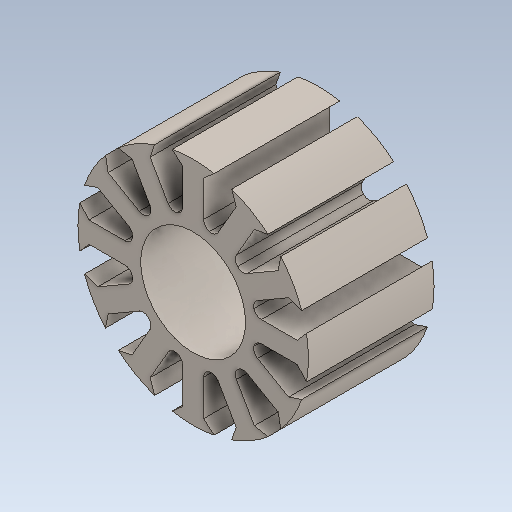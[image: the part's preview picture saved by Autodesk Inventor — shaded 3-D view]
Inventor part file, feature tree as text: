
AUTODESK INVENTOR PART (.ipt)
format: ipt  version: 2021 (Build 250183000, 183)  size: 216,576 bytes
history: mixed  units: mm
features: other x1, fillet x1, imported_body x1
ambient origin geometry x8: Origin, YZ Plane, XZ Plane, XY Plane, X Axis, Y Axis, Z Axis, Center Point
bodies: Body1 (imported_parasolid)
feature tree (3):
  other  "솔리드1"
  fillet  "Fillet4"  [1 undecoded]
  imported_body  NMx_Import_Brep_tag  [imported B-rep: ~87 faces, bbox_mm=[21.633308, 21.633308, 12.0]]
note: 1 required parameter value undecoded (feature->parameter linkage not recoverable at this tier; creation-order binding heuristic only, values carry confidence <= 0.55)
